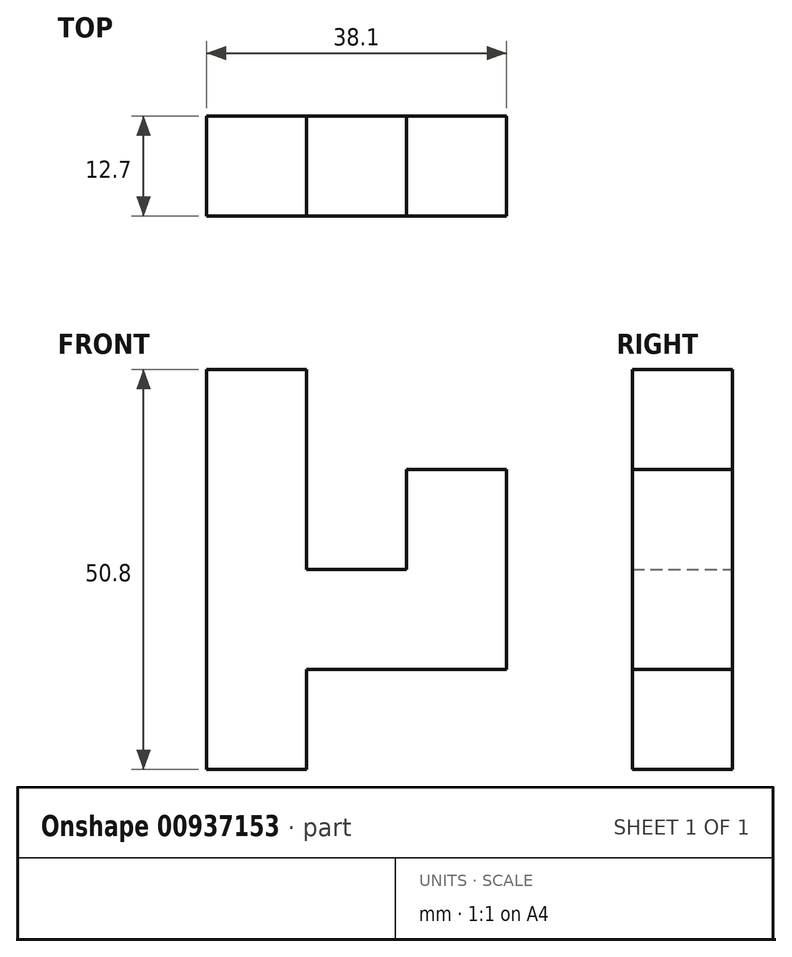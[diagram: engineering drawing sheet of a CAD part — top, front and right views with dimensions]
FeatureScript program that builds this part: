
annotation { "Feature Type Name" : "Feature", "Feature Type Description" : "" }
export const myFeature = defineFeature(function(context is Context, id is Id, definition is map)
    precondition{}
    {
        {
            var Q0;
            Q0=qCreatedBy(makeId("Front.planeOp"),FACE);
            var sketch = newSketch(context, id + "F0", { "sketchPlane" : qUnion([Q0])});
            skLineSegment(sketch, "E0.bottom", {"start": v(-55.6, 53.3) * mm, "end": v(-42.9, 53.3) * mm});
            skLineSegment(sketch, "E0.top", {"start": v(-55.6, 40.6) * mm, "end": v(-42.9, 40.6) * mm});
            skLineSegment(sketch, "E0.left", {"start": v(-55.6, 53.3) * mm, "end": v(-55.6, 40.6) * mm});
            skLineSegment(sketch, "E0.right", {"start": v(-42.9, 53.3) * mm, "end": v(-42.9, 40.6) * mm});
            skLineSegment(sketch, "E1.top", {"start": v(-55.6, 27.9) * mm, "end": v(-42.9, 27.9) * mm});
            skLineSegment(sketch, "E1.left", {"start": v(-55.6, 40.6) * mm, "end": v(-55.6, 27.9) * mm});
            skLineSegment(sketch, "E1.right", {"start": v(-42.9, 40.6) * mm, "end": v(-42.9, 27.9) * mm});
            skLineSegment(sketch, "E2.top", {"start": v(-55.6, 15.2) * mm, "end": v(-42.9, 15.2) * mm});
            skLineSegment(sketch, "E2.left", {"start": v(-55.6, 27.9) * mm, "end": v(-55.6, 15.2) * mm});
            skLineSegment(sketch, "E2.right", {"start": v(-42.9, 27.9) * mm, "end": v(-42.9, 15.2) * mm});
            skLineSegment(sketch, "E3.top", {"start": v(-55.6, 2.5) * mm, "end": v(-42.9, 2.5) * mm});
            skLineSegment(sketch, "E3.left", {"start": v(-55.6, 15.2) * mm, "end": v(-55.6, 2.5) * mm});
            skLineSegment(sketch, "E3.right", {"start": v(-42.9, 15.2) * mm, "end": v(-42.9, 2.5) * mm});
            skLineSegment(sketch, "E4.bottom", {"start": v(-42.9, 27.9) * mm, "end": v(-30.2, 27.9) * mm});
            skLineSegment(sketch, "E4.top", {"start": v(-42.9, 15.2) * mm, "end": v(-30.2, 15.2) * mm});
            skLineSegment(sketch, "E4.right", {"start": v(-30.2, 27.9) * mm, "end": v(-30.2, 15.2) * mm});
            skLineSegment(sketch, "E5.bottom", {"start": v(-30.2, 27.9) * mm, "end": v(-17.5, 27.9) * mm});
            skLineSegment(sketch, "E5.top", {"start": v(-30.2, 15.2) * mm, "end": v(-17.5, 15.2) * mm});
            skLineSegment(sketch, "E5.right", {"start": v(-17.5, 27.9) * mm, "end": v(-17.5, 15.2) * mm});
            skLineSegment(sketch, "E6.bottom", {"start": v(-17.5, 27.9) * mm, "end": v(-30.2, 27.9) * mm});
            skLineSegment(sketch, "E6.top", {"start": v(-17.5, 40.6) * mm, "end": v(-30.2, 40.6) * mm});
            skLineSegment(sketch, "E6.left", {"start": v(-17.5, 27.9) * mm, "end": v(-17.5, 40.6) * mm});
            skLineSegment(sketch, "E6.right", {"start": v(-30.2, 27.9) * mm, "end": v(-30.2, 40.6) * mm});
            skSolve(sketch);
        }
        {
            var Q0;
            Q0 = qSketchRegion(id + "F0", true);
            extrude(context, id + "F1", {"entities" : qUnion([Q0]), "endBound" : BoundingType.SYMMETRIC, "depth" : 12.7 * mm, "offsetDistance" : 25.4 * mm});
        }
    });
